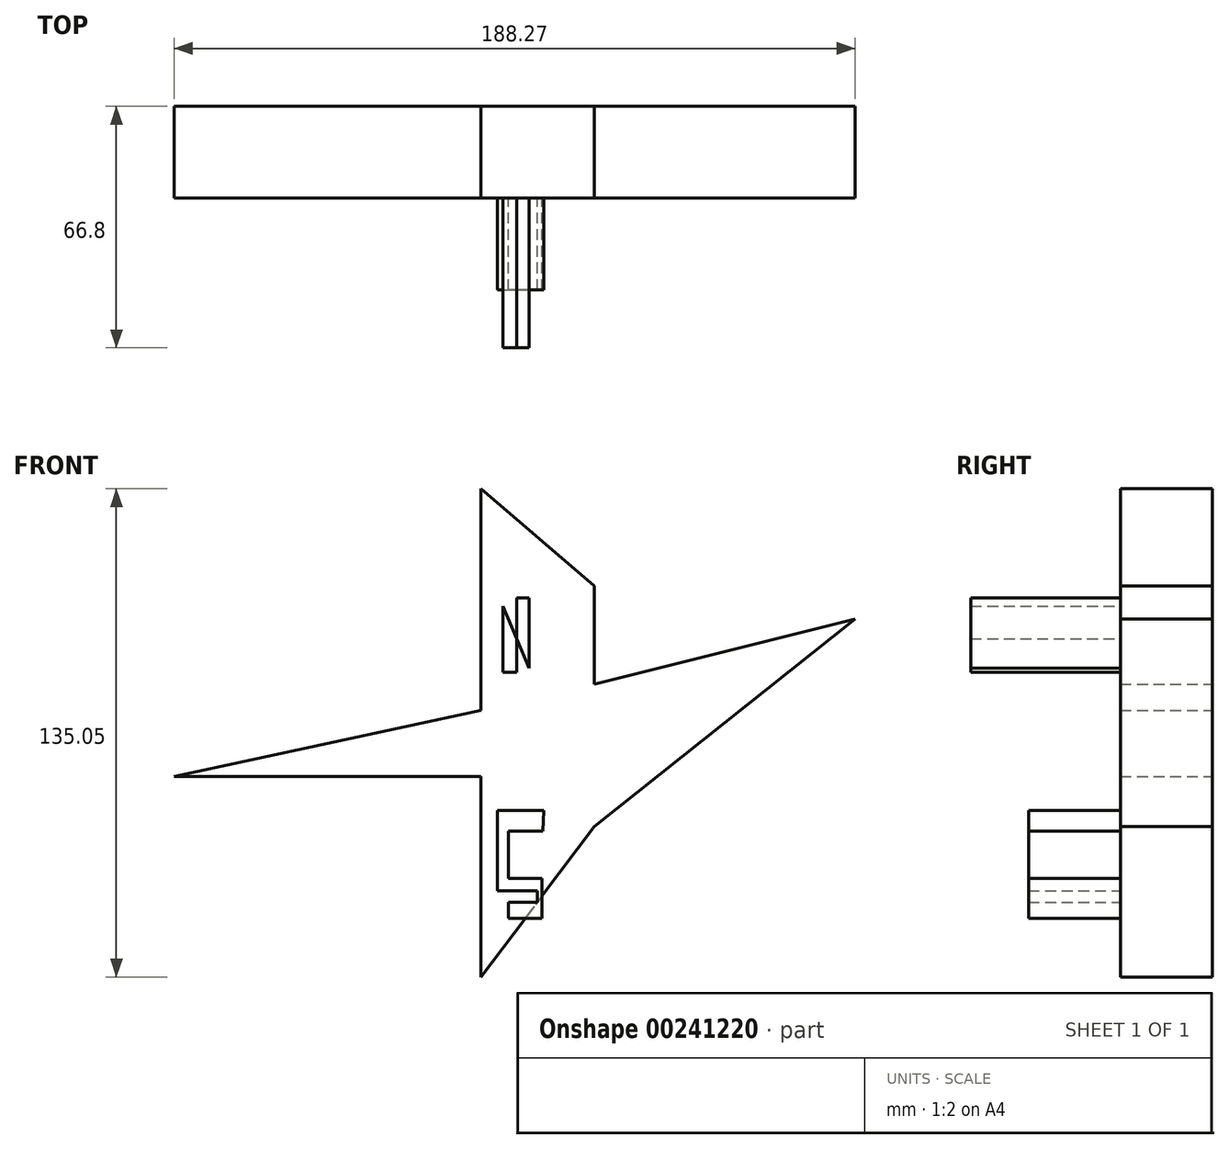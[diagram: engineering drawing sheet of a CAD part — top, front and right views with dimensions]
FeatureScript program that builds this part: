
annotation { "Feature Type Name" : "Feature", "Feature Type Description" : "" }
export const myFeature = defineFeature(function(context is Context, id is Id, definition is map)
    precondition{}
    {
        {
            var Q0;
            Q0=qCreatedBy(makeId("Front.planeOp"),FACE);
            var sketch = newSketch(context, id + "F0", { "sketchPlane" : qUnion([Q0])});
            skLineSegment(sketch, "E0", {"start": v(0, 64.33) * mm, "end": v(31.37, 37.4) * mm});
            skLineSegment(sketch, "E1", {"start": v(31.37, 37.4) * mm, "end": v(31.37, 10.3) * mm});
            skLineSegment(sketch, "E2", {"start": v(31.37, 10.3) * mm, "end": v(103.47, 28.32) * mm});
            skLineSegment(sketch, "E3", {"start": v(103.47, 28.32) * mm, "end": v(31.37, -29.16) * mm});
            skLineSegment(sketch, "E4", {"start": v(31.37, -29.16) * mm, "end": v(0, -70.72) * mm});
            skLineSegment(sketch, "E5", {"start": v(0, -70.72) * mm, "end": v(0, -15.25) * mm});
            skLineSegment(sketch, "E6", {"start": v(0, -15.25) * mm, "end": v(-84.8, -15.25) * mm});
            skLineSegment(sketch, "E7", {"start": v(0, 64.33) * mm, "end": v(0, 3.05) * mm});
            skLineSegment(sketch, "E8", {"start": v(-84.8, -15.25) * mm, "end": v(0, 3.05) * mm});
            skSolve(sketch);
        }
        {
            var Q0;
            Q0=makeQuery(id+"F0.imprint","IMPRINT",FACE,{"disambiguationData":[TD([[makeQuery(id+"F0.imprint","IMPRINT",EDGE,{"derivedFrom":sQuery(id+"F0.wireOp",EDGE,"E0")}),-1.0]])]});
            extrude(context, id + "F1", {"entities" : qUnion([Q0]), "depth" : 25.4 * mm});
        }
        {
            var Q0;
            Q0=makeQuery(id+"F1.opExtrude","CAP_FACE",FACE,{"disambiguationData":[OSD([sQuery(id+"F0.wireOp",EDGE,"E0"),sQuery(id+"F0.wireOp",EDGE,"E1"),sQuery(id+"F0.wireOp",EDGE,"E2"),sQuery(id+"F0.wireOp",EDGE,"E3"),sQuery(id+"F0.wireOp",EDGE,"E4"),sQuery(id+"F0.wireOp",EDGE,"E5"),sQuery(id+"F0.wireOp",EDGE,"E6"),sQuery(id+"F0.wireOp",EDGE,"E7"),sQuery(id+"F0.wireOp",EDGE,"E8")])],"isStart":false});
            var sketch = newSketch(context, id + "F2", { "sketchPlane" : qUnion([Q0])});
            skLineSegment(sketch, "E9", {"start": v(6.1, 13.5) * mm, "end": v(6.1, 31.8) * mm});
            skLineSegment(sketch, "E10", {"start": v(6.1, 31.8) * mm, "end": v(13.36, 14.67) * mm});
            skLineSegment(sketch, "E11", {"start": v(13.36, 14.67) * mm, "end": v(13.36, 34.12) * mm});
            skLineSegment(sketch, "E12", {"start": v(9.87, 34.12) * mm, "end": v(9.87, 22.9) * mm});
            skLineSegment(sketch, "E13", {"start": v(9.87, 22.9) * mm, "end": v(9.87, 34.12) * mm});
            skLineSegment(sketch, "E14", {"start": v(13.36, 34.12) * mm, "end": v(9.87, 34.12) * mm});
            skLineSegment(sketch, "E15", {"start": v(6.1, 13.5) * mm, "end": v(9.87, 13.5) * mm});
            skLineSegment(sketch, "E16", {"start": v(9.87, 13.5) * mm, "end": v(9.87, 22.9) * mm});
            skSolve(sketch);
        }
        {
            var Q0;
            {var subQ0=sQuery(id+"F2.wireOp",EDGE,"E11");Q0=makeQuery(id+"F2.imprint","IMPRINT",FACE,{"disambiguationData":[TD([[makeQuery(id+"F2.imprint","IMPRINT",EDGE,{"derivedFrom":subQ0}),1.0]])]});}
            var Q1;
            {var subQ0=sQuery(id+"F2.wireOp",EDGE,"E9");Q1=makeQuery(id+"F2.imprint","IMPRINT",FACE,{"disambiguationData":[TD([[makeQuery(id+"F2.imprint","IMPRINT",EDGE,{"derivedFrom":subQ0}),-1.0]])]});}
            extrude(context, id + "F3", {"entities" : qUnion([Q0, Q1]), "depth" : 41.4 * mm});
        }
        {
            var Q0;
            Q0=makeQuery(id+"F1.opExtrude","CAP_FACE",FACE,{"disambiguationData":[OSD([sQuery(id+"F0.wireOp",EDGE,"E0"),sQuery(id+"F0.wireOp",EDGE,"E1"),sQuery(id+"F0.wireOp",EDGE,"E2"),sQuery(id+"F0.wireOp",EDGE,"E3"),sQuery(id+"F0.wireOp",EDGE,"E4"),sQuery(id+"F0.wireOp",EDGE,"E5"),sQuery(id+"F0.wireOp",EDGE,"E6"),sQuery(id+"F0.wireOp",EDGE,"E7"),sQuery(id+"F0.wireOp",EDGE,"E8")])],"isStart":false});
            var sketch = newSketch(context, id + "F4", { "sketchPlane" : qUnion([Q0])});
            skLineSegment(sketch, "E17", {"start": v(17.2, -30.35) * mm, "end": v(7.59, -30.35) * mm});
            skLineSegment(sketch, "E18", {"start": v(7.59, -30.35) * mm, "end": v(7.59, -38.03) * mm});
            skLineSegment(sketch, "E19", {"start": v(7.59, -38.03) * mm, "end": v(7.59, -43.42) * mm});
            skLineSegment(sketch, "E20", {"start": v(7.59, -43.42) * mm, "end": v(16.91, -43.42) * mm});
            skLineSegment(sketch, "E21", {"start": v(16.91, -43.42) * mm, "end": v(16.91, -54.45) * mm});
            skLineSegment(sketch, "E22", {"start": v(16.91, -54.45) * mm, "end": v(7.59, -54.45) * mm});
            skLineSegment(sketch, "E23", {"start": v(7.59, -54.45) * mm, "end": v(7.59, -50.09) * mm});
            skLineSegment(sketch, "E24", {"start": v(7.59, -50.09) * mm, "end": v(15.57, -50.09) * mm});
            skLineSegment(sketch, "E25", {"start": v(15.57, -50.09) * mm, "end": v(15.68, -46.9) * mm});
            skPoint(sketch, "E25.endSnap0", {"position": v(15.68, -49.94) * mm});
            skLineSegment(sketch, "E26", {"start": v(15.68, -46.9) * mm, "end": v(7.59, -46.9) * mm});
            skLineSegment(sketch, "E27", {"start": v(7.59, -46.9) * mm, "end": v(4.54, -46.9) * mm});
            skLineSegment(sketch, "E28", {"start": v(4.54, -46.9) * mm, "end": v(4.54, -29.16) * mm});
            skLineSegment(sketch, "E29", {"start": v(4.54, -29.16) * mm, "end": v(4.54, -24.63) * mm});
            skLineSegment(sketch, "E30", {"start": v(4.54, -24.63) * mm, "end": v(17.35, -24.63) * mm});
            skLineSegment(sketch, "E31", {"start": v(17.2, -30.35) * mm, "end": v(17.35, -24.63) * mm});
            skPoint(sketch, "E32", {"position": v(4.54, -38.03) * mm});
            skSolve(sketch);
        }
        {
            var Q0;
            Q0=makeQuery(id+"F4.imprint","IMPRINT",FACE,{"disambiguationData":[TD([[makeQuery(id+"F4.imprint","IMPRINT",EDGE,{"derivedFrom":sQuery(id+"F4.wireOp",EDGE,"E17")}),-1.0]])]});
            var Q1;
            {var subQ0=sQuery(id+"F4.wireOp",EDGE,"E22");var subQ1=sQuery(id+"F4.wireOp",EDGE,"E21");var subQ2=makeQuery(id+"F4.imprint","INTERSECT",VERTEX,{"derivedFrom":[subQ1,subQ0]});Q1=makeQuery(id+"F4.imprint","IMPRINT",FACE,{"disambiguationData":[TD([[makeQuery(id+"F4.imprint","IMPRINT",EDGE,{"disambiguationData":[TD([[subQ2,1.0]])],"derivedFrom":subQ1}),-1.0]])]});}
            var Q2;
            {var subQ0=sQuery(id+"F4.wireOp",EDGE,"E23");Q2=makeQuery(id+"F4.imprint","IMPRINT",FACE,{"disambiguationData":[TD([[makeQuery(id+"F4.imprint","IMPRINT",EDGE,{"derivedFrom":subQ0}),-1.0]])]});}
            extrude(context, id + "F5", {"entities" : qUnion([Q0, Q1, Q2]), "depth" : 25.4 * mm});
        }
    });
